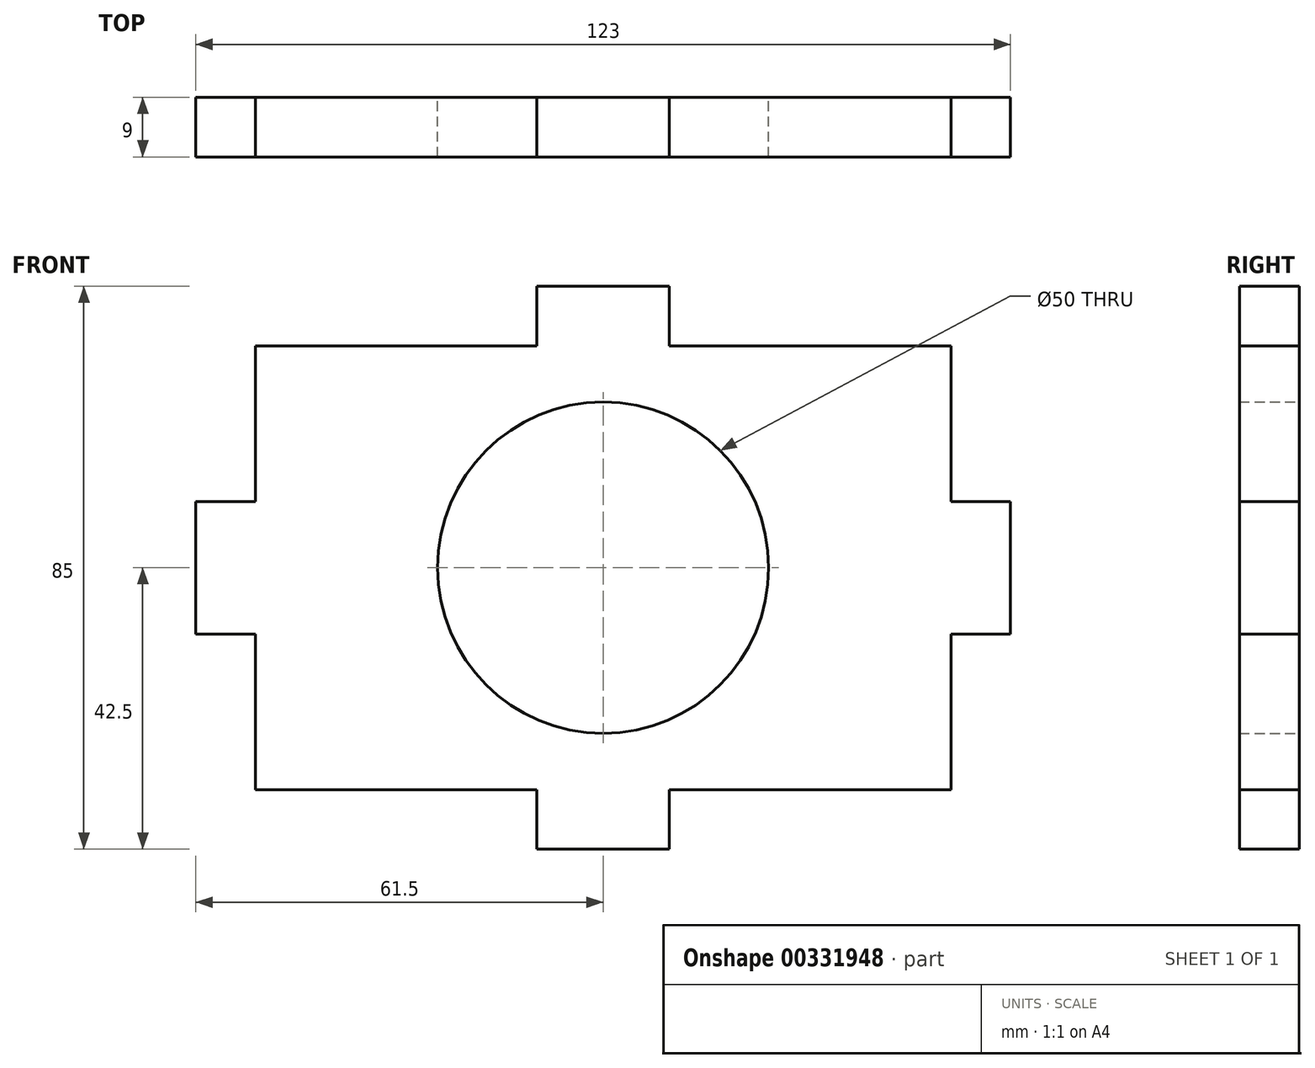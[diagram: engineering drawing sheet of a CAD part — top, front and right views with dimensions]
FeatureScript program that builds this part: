
annotation { "Feature Type Name" : "Feature", "Feature Type Description" : "" }
export const myFeature = defineFeature(function(context is Context, id is Id, definition is map)
    precondition{}
    {
        {
            var Q0;
            Q0=qCreatedBy(makeId("Front.planeOp"),FACE);
            var sketch = newSketch(context, id + "F0", { "sketchPlane" : qUnion([Q0])});
            skLineSegment(sketch, "E0.top", {"start": v(10, -42.5) * mm, "end": v(-10, -42.5) * mm});
            skLineSegment(sketch, "E0.left", {"start": v(61.5, 10) * mm, "end": v(61.5, -10) * mm});
            skLineSegment(sketch, "E0.right", {"start": v(-61.5, 10) * mm, "end": v(-61.5, -10) * mm});
            skPoint(sketch, "E0.middle", {"position": v(0, 0) * mm});
            skLineSegment(sketch, "E1", {"start": v(-52.5, 33.5) * mm, "end": v(-10, 33.5) * mm, "construction": true});
            skLineSegment(sketch, "E2", {"start": v(-10, 42.5) * mm, "end": v(-10, 33.5) * mm, "construction": true});
            skLineSegment(sketch, "E3", {"start": v(10, 42.5) * mm, "end": v(10, 33.5) * mm, "construction": true});
            skLineSegment(sketch, "E4", {"start": v(-61.5, 10) * mm, "end": v(-52.5, 10) * mm});
            skLineSegment(sketch, "E5", {"start": v(-61.5, -10) * mm, "end": v(-52.5, -10) * mm, "construction": true});
            skLineSegment(sketch, "E6", {"start": v(-52.5, 33.5) * mm, "end": v(-52.5, 10) * mm});
            skLineSegment(sketch, "E7", {"start": v(52.5, 33.5) * mm, "end": v(52.5, 10) * mm});
            skLineSegment(sketch, "E8", {"start": v(-52.5, 33.5) * mm, "end": v(-10, 33.5) * mm});
            skLineSegment(sketch, "E9", {"start": v(-10, 33.5) * mm, "end": v(-10, 42.5) * mm});
            skLineSegment(sketch, "E10", {"start": v(52.5, 33.5) * mm, "end": v(10, 33.5) * mm});
            skLineSegment(sketch, "E11", {"start": v(10, 33.5) * mm, "end": v(10, 42.5) * mm});
            skPoint(sketch, "E12.orphan", {"position": v(-61.5, 42.5) * mm});
            skLineSegment(sketch, "E13.trimOffspring", {"start": v(10, 42.5) * mm, "end": v(-10, 42.5) * mm});
            skPoint(sketch, "E14.orphan", {"position": v(61.5, 42.5) * mm});
            skLineSegment(sketch, "E15.trimOffspring", {"start": v(10, 33.5) * mm, "end": v(52.5, 33.5) * mm, "construction": true});
            skPoint(sketch, "E16.orphan", {"position": v(-61.5, 33.5) * mm});
            skPoint(sketch, "E17.orphan", {"position": v(-61.5, -42.5) * mm});
            skLineSegment(sketch, "E18", {"start": v(-61.5, -10) * mm, "end": v(-52.5, -10) * mm});
            skLineSegment(sketch, "E19", {"start": v(61.5, -10) * mm, "end": v(52.5, -10) * mm});
            skPoint(sketch, "E20.orphan", {"position": v(61.5, -42.5) * mm});
            skLineSegment(sketch, "E21", {"start": v(-52.5, -33.5) * mm, "end": v(-10, -33.5) * mm});
            skLineSegment(sketch, "E22", {"start": v(-10, -33.5) * mm, "end": v(-10, -42.5) * mm});
            skLineSegment(sketch, "E23", {"start": v(10, -33.5) * mm, "end": v(10, -42.5) * mm});
            skLineSegment(sketch, "E24.trimOffspring", {"start": v(-10, -33.5) * mm, "end": v(-10, -42.5) * mm, "construction": true});
            skLineSegment(sketch, "E25.trimOffspring", {"start": v(52.5, -10) * mm, "end": v(61.5, -10) * mm, "construction": true});
            skLineSegment(sketch, "E26.trimOffspring", {"start": v(52.5, 10) * mm, "end": v(61.5, 10) * mm});
            skLineSegment(sketch, "E27.trimOffspring", {"start": v(10, -33.5) * mm, "end": v(10, -42.5) * mm, "construction": true});
            skLineSegment(sketch, "E28.trimOffspring", {"start": v(52.5, -10) * mm, "end": v(52.5, -33.5) * mm});
            skLineSegment(sketch, "E29", {"start": v(10, -33.5) * mm, "end": v(52.5, -33.5) * mm});
            skPoint(sketch, "E30.orphan", {"position": v(52.5, -42.5) * mm});
            skPoint(sketch, "E31.orphan", {"position": v(-52.5, -42.5) * mm});
            skLineSegment(sketch, "E32.trimOffspring", {"start": v(-52.5, -10) * mm, "end": v(-52.5, -33.5) * mm});
            skPoint(sketch, "E33.orphan", {"position": v(-61.5, 0) * mm});
            skPoint(sketch, "E34.end.orphan", {"position": v(61.5, 0) * mm});
            skSolve(sketch);
        }
        {
            var Q0;
            Q0=makeQuery(id+"F0.imprint","IMPRINT",FACE,{"disambiguationData":[TD([[makeQuery(id+"F0.imprint","IMPRINT",EDGE,{"derivedFrom":sQuery(id+"F0.wireOp",EDGE,"E0.top")}),-1.0]])]});
            extrude(context, id + "F1", {"entities" : qUnion([Q0]), "depth" : 9 * mm});
        }
        {
            var Q0;
            Q0=qCreatedBy(makeId("Front.planeOp"),FACE);
            var sketch = newSketch(context, id + "F2", { "sketchPlane" : qUnion([Q0])});
            skCircle(sketch, "E35", {"center": v(0, 0) * mm, "radius": 25 * mm});
            skSolve(sketch);
        }
        {
            var Q0;
            Q0=sQuery(id+"F2.wireOp",VERTEX,"E35.center");
            var Q1;
            Q1=makeQuery(id+"F1.opExtrude","SWEPT_BODY",BODY,{"disambiguationData":[OSD([sQuery(id+"F0.wireOp",EDGE,"E0.top"),sQuery(id+"F0.wireOp",EDGE,"E0.left"),sQuery(id+"F0.wireOp",EDGE,"E0.right"),sQuery(id+"F0.wireOp",EDGE,"E4"),sQuery(id+"F0.wireOp",EDGE,"E6"),sQuery(id+"F0.wireOp",EDGE,"E7"),sQuery(id+"F0.wireOp",EDGE,"E8"),sQuery(id+"F0.wireOp",EDGE,"E9"),sQuery(id+"F0.wireOp",EDGE,"E10"),sQuery(id+"F0.wireOp",EDGE,"E11"),sQuery(id+"F0.wireOp",EDGE,"E13.trimOffspring"),sQuery(id+"F0.wireOp",EDGE,"E18"),sQuery(id+"F0.wireOp",EDGE,"E19"),sQuery(id+"F0.wireOp",EDGE,"E21"),sQuery(id+"F0.wireOp",EDGE,"E22"),sQuery(id+"F0.wireOp",EDGE,"E23"),sQuery(id+"F0.wireOp",EDGE,"E26.trimOffspring"),sQuery(id+"F0.wireOp",EDGE,"E28.trimOffspring"),sQuery(id+"F0.wireOp",EDGE,"E29"),sQuery(id+"F0.wireOp",EDGE,"E32.trimOffspring")])]});
            hole(context, id + "F3", {"style" : HoleStyle.SIMPLE, "endStyle" : HoleEndStyle.THROUGH, "oppositeDirection" : true, "holeDiameter" : 50 * mm, "tappedDepth" : 12 * mm, "tapClearance" : 3, "locations" : qUnion([Q0]), "scope" : qUnion([Q1])});
        }
    });
